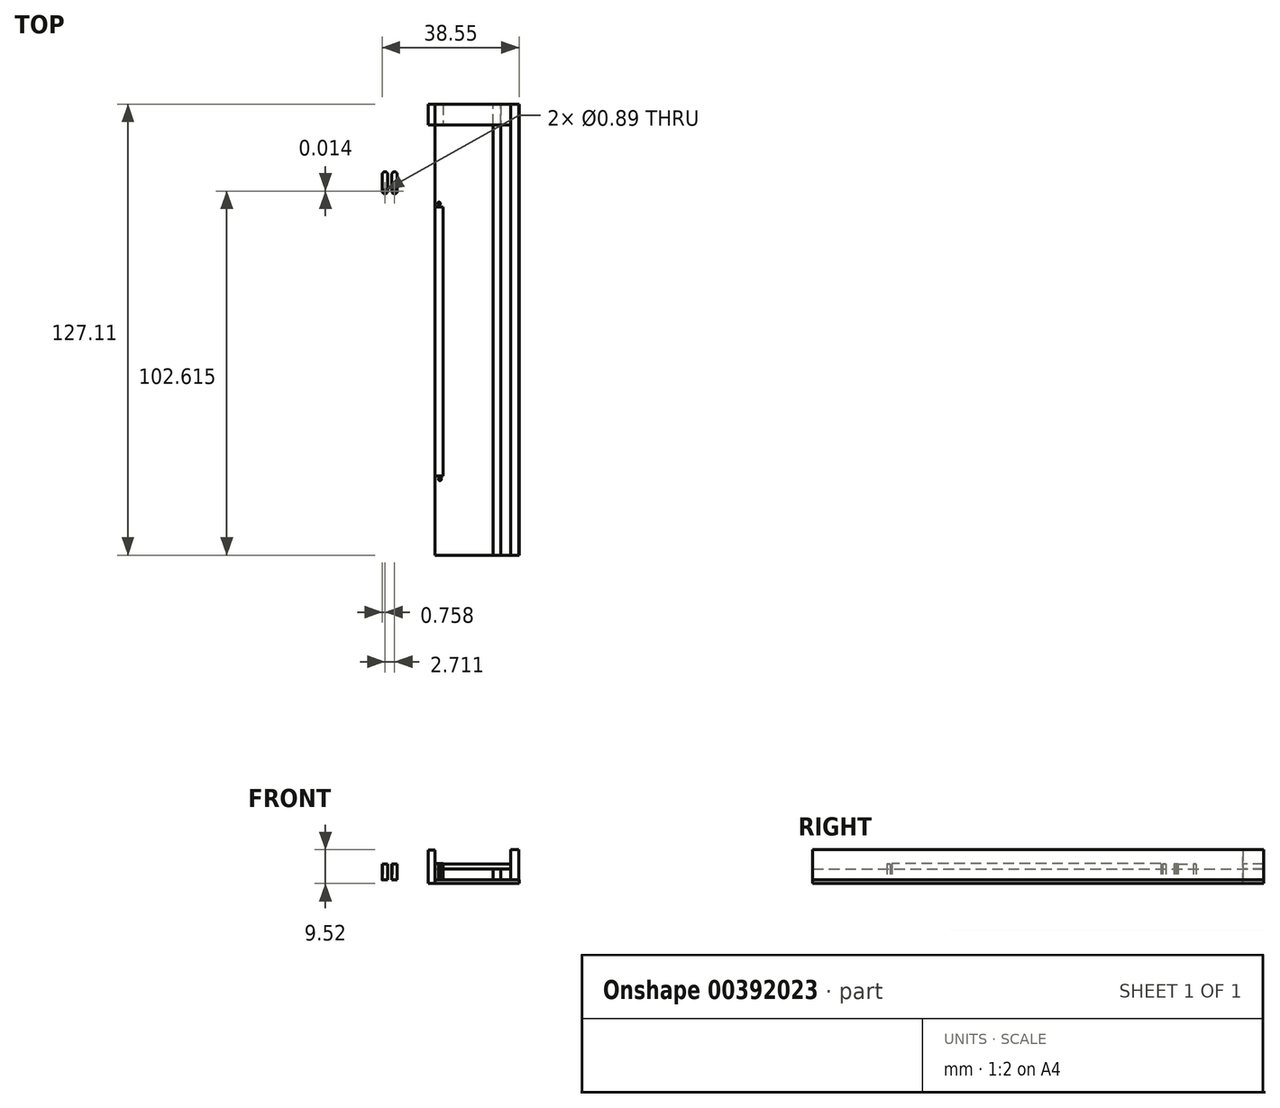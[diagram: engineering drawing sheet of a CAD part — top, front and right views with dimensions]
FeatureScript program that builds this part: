
annotation { "Feature Type Name" : "Feature", "Feature Type Description" : "" }
export const myFeature = defineFeature(function(context is Context, id is Id, definition is map)
    precondition{}
    {
        {
            var Q0;
            Q0=qCreatedBy(makeId("Top.planeOp"),FACE);
            var sketch = newSketch(context, id + "F0", { "sketchPlane" : qUnion([Q0])});
            skLineSegment(sketch, "E0.bottom", {"start": v(-12.76, 61.7) * mm, "end": v(12.87, 61.7) * mm});
            skLineSegment(sketch, "E0.top", {"start": v(-12.76, -65.4) * mm, "end": v(12.87, -65.4) * mm});
            skLineSegment(sketch, "E0.left", {"start": v(-12.76, 61.7) * mm, "end": v(-12.76, -65.4) * mm});
            skLineSegment(sketch, "E0.right", {"start": v(12.87, 61.7) * mm, "end": v(12.87, -65.4) * mm});
            skLineSegment(sketch, "E1", {"start": v(-10.88, 61.7) * mm, "end": v(-10.88, -65.4) * mm});
            skLineSegment(sketch, "E2", {"start": v(10.5, 61.7) * mm, "end": v(10.5, -65.4) * mm});
            skLineSegment(sketch, "E3", {"start": v(7.72, 61.7) * mm, "end": v(7.72, -65.4) * mm});
            skLineSegment(sketch, "E4", {"start": v(5.47, 61.7) * mm, "end": v(5.47, -65.4) * mm});
            skLineSegment(sketch, "E5", {"start": v(-8.47, 61.7) * mm, "end": v(-8.47, 39.44) * mm});
            skLineSegment(sketch, "E6.top", {"start": v(-12.76, 55.9) * mm, "end": v(12.87, 55.9) * mm});
            skLineSegment(sketch, "E6.left", {"start": v(-12.76, 61.7) * mm, "end": v(-12.76, 55.9) * mm});
            skLineSegment(sketch, "E6.right", {"start": v(12.87, 61.7) * mm, "end": v(12.87, 55.9) * mm});
            skLineSegment(sketch, "E7", {"start": v(-8.47, 39.44) * mm, "end": v(-10.88, 39.44) * mm});
            skLineSegment(sketch, "E8", {"start": v(-8.47, 32.73) * mm, "end": v(-10.88, 32.73) * mm});
            skLineSegment(sketch, "E9", {"start": v(-8.47, -43.05) * mm, "end": v(-10.88, -43.05) * mm});
            skLineSegment(sketch, "E10", {"start": v(-8.47, -49.75) * mm, "end": v(-10.88, -49.75) * mm});
            skLineSegment(sketch, "E11.trimOffspring", {"start": v(-8.47, 32.73) * mm, "end": v(-8.47, -43.05) * mm});
            skLineSegment(sketch, "E12.trimOffspring", {"start": v(-8.47, -49.75) * mm, "end": v(-8.47, -65.4) * mm});
            skCircle(sketch, "E13", {"center": v(-9.7, 33.72) * mm, "radius": 0.44 * mm});
            skArc(sketch, "E14", {"start": v(-10.46, 33.78) * mm, "mid": v(-9.7, 32.96) * mm, "end": v(-8.95, 33.78) * mm});
            skLineSegment(sketch, "E15", {"start": v(-8.95, 33.78) * mm, "end": v(-8.95, 38.42) * mm});
            skLineSegment(sketch, "E16", {"start": v(-10.46, 33.78) * mm, "end": v(-10.46, 38.4) * mm});
            skArc(sketch, "E17", {"start": v(-8.95, 38.42) * mm, "mid": v(-9.71, 39.18) * mm, "end": v(-10.46, 38.4) * mm});
            skCircle(sketch, "E18", {"center": v(-9.7, 33.72) * mm, "radius": 0.41 * mm});
            skCircle(sketch, "E19", {"center": v(-9.45, -43.97) * mm, "radius": 0.44 * mm});
            skArc(sketch, "E20", {"start": v(-8.7, -44.03) * mm, "mid": v(-9.44, -43.21) * mm, "end": v(-10.2, -44.02) * mm});
            skLineSegment(sketch, "E21", {"start": v(-10.2, -44.02) * mm, "end": v(-10.2, -48.67) * mm});
            skLineSegment(sketch, "E22", {"start": v(-8.7, -44.03) * mm, "end": v(-8.7, -48.65) * mm});
            skArc(sketch, "E23", {"start": v(-10.2, -48.67) * mm, "mid": v(-9.44, -49.43) * mm, "end": v(-8.7, -48.65) * mm});
            skCircle(sketch, "E24", {"center": v(-9.45, -43.97) * mm, "radius": 0.41 * mm});
            skSolve(sketch);
        }
        {
            var Q0;
            Q0=qCreatedBy(makeId("Top.planeOp"),FACE);
            var sketch = newSketch(context, id + "F1", { "sketchPlane" : qUnion([Q0])});
            skCircle(sketch, "E25", {"center": v(-24.92, 37.23) * mm, "radius": 0.44 * mm});
            skArc(sketch, "E26", {"start": v(-25.68, 37.3) * mm, "mid": v(-24.93, 36.47) * mm, "end": v(-24.17, 37.28) * mm});
            skLineSegment(sketch, "E27", {"start": v(-24.17, 37.28) * mm, "end": v(-24.17, 41.93) * mm});
            skLineSegment(sketch, "E28", {"start": v(-25.68, 37.3) * mm, "end": v(-25.68, 41.9) * mm});
            skArc(sketch, "E29", {"start": v(-24.17, 41.93) * mm, "mid": v(-24.93, 42.69) * mm, "end": v(-25.68, 41.9) * mm});
            skCircle(sketch, "E30", {"center": v(-22.21, 37.22) * mm, "radius": 0.44 * mm});
            skArc(sketch, "E31", {"start": v(-22.97, 37.28) * mm, "mid": v(-22.22, 36.46) * mm, "end": v(-21.46, 37.27) * mm});
            skLineSegment(sketch, "E32", {"start": v(-21.46, 37.27) * mm, "end": v(-21.46, 41.92) * mm});
            skLineSegment(sketch, "E33", {"start": v(-22.97, 37.28) * mm, "end": v(-22.97, 41.9) * mm});
            skArc(sketch, "E34", {"start": v(-21.46, 41.92) * mm, "mid": v(-22.22, 42.67) * mm, "end": v(-22.97, 41.9) * mm});
            skSolve(sketch);
        }
        {
            var Q0;
            Q0=qCreatedBy(makeId("Right.planeOp"),FACE);
            var sketch = newSketch(context, id + "F2", { "sketchPlane" : qUnion([Q0])});
            skLineSegment(sketch, "E35.bottom", {"start": v(61.7, 8.5) * mm, "end": v(-65.36, 8.5) * mm});
            skLineSegment(sketch, "E35.top", {"start": v(61.7, 0) * mm, "end": v(-65.36, 0) * mm});
            skLineSegment(sketch, "E35.left", {"start": v(61.7, 8.5) * mm, "end": v(61.7, 0) * mm});
            skLineSegment(sketch, "E35.right", {"start": v(-65.36, 8.5) * mm, "end": v(-65.36, 0) * mm});
            skSolve(sketch);
        }
        {
            var Q0;
            Q0=qCreatedBy(makeId("Front.planeOp"),FACE);
            var sketch = newSketch(context, id + "F3", { "sketchPlane" : qUnion([Q0])});
            skLineSegment(sketch, "E36.bottom", {"start": v(7.75, 0) * mm, "end": v(5.5, 0) * mm});
            skLineSegment(sketch, "E36.right", {"start": v(5.5, 0) * mm, "end": v(5.5, 3.08) * mm});
            skLineSegment(sketch, "E37", {"start": v(7.75, 0) * mm, "end": v(7.75, 3.08) * mm});
            skLineSegment(sketch, "E38.trimOffspring", {"start": v(7.75, 3.08) * mm, "end": v(5.5, 3.08) * mm});
            skLineSegment(sketch, "E39.bottom", {"start": v(-8.47, 0) * mm, "end": v(-10.87, 0) * mm});
            skLineSegment(sketch, "E39.top", {"start": v(-8.47, 3.08) * mm, "end": v(-10.87, 3.08) * mm});
            skLineSegment(sketch, "E39.left", {"start": v(-8.47, 0) * mm, "end": v(-8.47, 3.08) * mm});
            skLineSegment(sketch, "E39.right", {"start": v(-10.87, 0) * mm, "end": v(-10.87, 3.08) * mm});
            skPoint(sketch, "E40.orphan", {"position": v(12.85, 0) * mm});
            skLineSegment(sketch, "E41.bottom", {"start": v(7.75, 3.08) * mm, "end": v(-10.87, 3.08) * mm});
            skLineSegment(sketch, "E41.top", {"start": v(7.75, 4.56) * mm, "end": v(-10.87, 4.56) * mm});
            skLineSegment(sketch, "E41.left", {"start": v(7.75, 3.08) * mm, "end": v(7.75, 4.56) * mm});
            skLineSegment(sketch, "E41.right", {"start": v(-10.87, 3.08) * mm, "end": v(-10.87, 4.56) * mm});
            skSolve(sketch);
        }
        {
            var Q0;
            Q0 = qSketchRegion(id + "F2", true);
            extrude(context, id + "F4", {"entities" : qUnion([Q0]), "depth" : 12.83 * mm, "hasSecondDirection" : true, "secondDirectionOppositeDirection" : false, "secondDirectionDepth" : 10.5 * mm});
        }
        {
            var Q0;
            Q0=makeQuery(id+"F3.imprint","IMPRINT",FACE,{"disambiguationData":[TD([[makeQuery(id+"F3.imprint","IMPRINT",EDGE,{"derivedFrom":sQuery(id+"F3.wireOp",EDGE,"E36.bottom")}),-1.0]])]});
            extrude(context, id + "F5", {"entities" : qUnion([Q0]), "depth" : 65.38 * mm, "hasSecondDirection" : true, "secondDirectionOppositeDirection" : true, "secondDirectionDepth" : 61.7 * mm});
        }
        {
            var Q0;
            Q0=makeQuery(id+"F0.imprint","IMPRINT",FACE,{"disambiguationData":[TD([[makeQuery(id+"F0.imprint","IMPRINT",EDGE,{"derivedFrom":sQuery(id+"F0.wireOp",EDGE,"E18")}),1.0]])]});
            var Q1;
            Q1=makeQuery(id+"F0.imprint","IMPRINT",FACE,{"disambiguationData":[TD([[makeQuery(id+"F0.imprint","IMPRINT",EDGE,{"derivedFrom":sQuery(id+"F0.wireOp",EDGE,"E13")}),-1.0]])]});
            var Q2;
            Q2=makeQuery(id+"F0.imprint","IMPRINT",FACE,{"disambiguationData":[TD([[makeQuery(id+"F0.imprint","IMPRINT",EDGE,{"derivedFrom":sQuery(id+"F0.wireOp",EDGE,"E13")}),1.0]])]});
            var Q3;
            {var subQ4=sQuery(id+"F0.wireOp",EDGE,"E0.left");Q3=makeQuery(id+"F0.imprint","IMPRINT",FACE,{"disambiguationData":[TD([[makeQuery(id+"F0.imprint","IMPRINT",EDGE,{"derivedFrom":subQ4}),1.0]])]});}
            var Q4;
            {var subQ0=sQuery(id+"F0.wireOp",EDGE,"E7");Q4=makeQuery(id+"F0.imprint","IMPRINT",FACE,{"disambiguationData":[TD([[makeQuery(id+"F0.imprint","IMPRINT",EDGE,{"derivedFrom":subQ0}),-1.0]])]});}
            var Q5;
            {var subQ0=sQuery(id+"F0.wireOp",EDGE,"E8");Q5=makeQuery(id+"F0.imprint","IMPRINT",FACE,{"disambiguationData":[TD([[makeQuery(id+"F0.imprint","IMPRINT",EDGE,{"derivedFrom":subQ0}),1.0]])]});}
            var Q6;
            {var subQ3=sQuery(id+"F0.wireOp",EDGE,"E7");Q6=makeQuery(id+"F0.imprint","IMPRINT",FACE,{"disambiguationData":[TD([[makeQuery(id+"F0.imprint","IMPRINT",EDGE,{"derivedFrom":subQ3}),1.0]])]});}
            var Q7;
            {var subQ0=sQuery(id+"F0.wireOp",EDGE,"E0.bottom");var subQ1=sQuery(id+"F0.wireOp",EDGE,"E4");var subQ2=makeQuery(id+"F0.imprint","INTERSECT",VERTEX,{"derivedFrom":[subQ1,subQ0]});Q7=makeQuery(id+"F0.imprint","IMPRINT",FACE,{"disambiguationData":[TD([[makeQuery(id+"F0.imprint","IMPRINT",EDGE,{"disambiguationData":[TD([[subQ2,-1.0]])],"derivedFrom":subQ1}),-1.0]])]});}
            var Q8;
            {var subQ0=sQuery(id+"F0.wireOp",EDGE,"E0.bottom");var subQ1=sQuery(id+"F0.wireOp",EDGE,"E1");var subQ2=makeQuery(id+"F0.imprint","INTERSECT",VERTEX,{"derivedFrom":[subQ1,subQ0]});Q8=makeQuery(id+"F0.imprint","IMPRINT",FACE,{"disambiguationData":[TD([[makeQuery(id+"F0.imprint","IMPRINT",EDGE,{"disambiguationData":[TD([[subQ2,-1.0]])],"derivedFrom":subQ1}),1.0]])]});}
            var Q9;
            {var subQ5=sQuery(id+"F0.wireOp",EDGE,"E6.left");Q9=makeQuery(id+"F0.imprint","IMPRINT",FACE,{"disambiguationData":[TD([[makeQuery(id+"F0.imprint","IMPRINT",EDGE,{"derivedFrom":subQ5}),1.0]])]});}
            var Q10;
            {var subQ0=sQuery(id+"F0.wireOp",EDGE,"E0.bottom");var subQ1=sQuery(id+"F0.wireOp",EDGE,"E3");var subQ2=makeQuery(id+"F0.imprint","INTERSECT",VERTEX,{"derivedFrom":[subQ1,subQ0]});Q10=makeQuery(id+"F0.imprint","IMPRINT",FACE,{"disambiguationData":[TD([[makeQuery(id+"F0.imprint","IMPRINT",EDGE,{"disambiguationData":[TD([[subQ2,-1.0]])],"derivedFrom":subQ1}),-1.0]])]});}
            var Q11;
            {var subQ0=sQuery(id+"F0.wireOp",EDGE,"E0.bottom");var subQ1=sQuery(id+"F0.wireOp",EDGE,"E2");var subQ2=makeQuery(id+"F0.imprint","INTERSECT",VERTEX,{"derivedFrom":[subQ1,subQ0]});Q11=makeQuery(id+"F0.imprint","IMPRINT",FACE,{"disambiguationData":[TD([[makeQuery(id+"F0.imprint","IMPRINT",EDGE,{"disambiguationData":[TD([[subQ2,-1.0]])],"derivedFrom":subQ1}),-1.0]])]});}
            var Q12;
            {var subQ0=sQuery(id+"F0.wireOp",EDGE,"E2");var subQ1=sQuery(id+"F0.wireOp",EDGE,"E0.top");var subQ2=makeQuery(id+"F0.imprint","INTERSECT",VERTEX,{"derivedFrom":[subQ1,subQ0]});Q12=makeQuery(id+"F0.imprint","IMPRINT",FACE,{"disambiguationData":[TD([[makeQuery(id+"F0.imprint","IMPRINT",EDGE,{"disambiguationData":[TD([[subQ2,1.0]])],"derivedFrom":subQ1}),1.0]])]});}
            var Q13;
            {var subQ0=sQuery(id+"F0.wireOp",EDGE,"E0.right");Q13=makeQuery(id+"F0.imprint","IMPRINT",FACE,{"disambiguationData":[TD([[makeQuery(id+"F0.imprint","IMPRINT",EDGE,{"derivedFrom":subQ0}),-1.0]])]});}
            var Q14;
            {var subQ5=sQuery(id+"F0.wireOp",EDGE,"E6.right");Q14=makeQuery(id+"F0.imprint","IMPRINT",FACE,{"disambiguationData":[TD([[makeQuery(id+"F0.imprint","IMPRINT",EDGE,{"derivedFrom":subQ5}),-1.0]])]});}
            var Q15;
            Q15=makeQuery(id+"F0.imprint","IMPRINT",FACE,{"disambiguationData":[TD([[makeQuery(id+"F0.imprint","IMPRINT",EDGE,{"derivedFrom":sQuery(id+"F0.wireOp",EDGE,"E19")}),-1.0]])]});
            var Q16;
            {var subQ4=sQuery(id+"F0.wireOp",EDGE,"E10");Q16=makeQuery(id+"F0.imprint","IMPRINT",FACE,{"disambiguationData":[TD([[makeQuery(id+"F0.imprint","IMPRINT",EDGE,{"derivedFrom":subQ4}),1.0]])]});}
            var Q17;
            Q17=makeQuery(id+"F0.imprint","IMPRINT",FACE,{"disambiguationData":[TD([[makeQuery(id+"F0.imprint","IMPRINT",EDGE,{"derivedFrom":sQuery(id+"F0.wireOp",EDGE,"E24")}),1.0]])]});
            var Q18;
            Q18=makeQuery(id+"F0.imprint","IMPRINT",FACE,{"disambiguationData":[TD([[makeQuery(id+"F0.imprint","IMPRINT",EDGE,{"derivedFrom":sQuery(id+"F0.wireOp",EDGE,"E19")}),1.0]])]});
            var Q19;
            {var subQ0=sQuery(id+"F0.wireOp",EDGE,"E3");var subQ1=sQuery(id+"F0.wireOp",EDGE,"E0.top");var subQ2=makeQuery(id+"F0.imprint","INTERSECT",VERTEX,{"derivedFrom":[subQ1,subQ0]});Q19=makeQuery(id+"F0.imprint","IMPRINT",FACE,{"disambiguationData":[TD([[makeQuery(id+"F0.imprint","IMPRINT",EDGE,{"disambiguationData":[TD([[subQ2,1.0]])],"derivedFrom":subQ1}),1.0]])]});}
            extrude(context, id + "F6", {"entities" : qUnion([Q0, Q1, Q2, Q3, Q4, Q5, Q6, Q7, Q8, Q9, Q10, Q11, Q12, Q13, Q14, Q15, Q16, Q17, Q18, Q19]), "oppositeDirection" : true, "depth" : 1.02 * mm});
        }
        {
            var Q0;
            {var subQ4=sQuery(id+"F0.wireOp",EDGE,"E0.left");Q0=makeQuery(id+"F0.imprint","IMPRINT",FACE,{"disambiguationData":[TD([[makeQuery(id+"F0.imprint","IMPRINT",EDGE,{"derivedFrom":subQ4}),1.0]])]});}
            var Q1;
            {var subQ5=sQuery(id+"F0.wireOp",EDGE,"E6.left");Q1=makeQuery(id+"F0.imprint","IMPRINT",FACE,{"disambiguationData":[TD([[makeQuery(id+"F0.imprint","IMPRINT",EDGE,{"derivedFrom":subQ5}),1.0]])]});}
            extrude(context, id + "F7", {"entities" : qUnion([Q0, Q1]), "operationType" : NewBodyOperationType.ADD, "depth" : 8.38 * mm});
        }
        {
            var Q0;
            Q0=makeQuery(id+"F0.imprint","IMPRINT",FACE,{"disambiguationData":[TD([[makeQuery(id+"F0.imprint","IMPRINT",EDGE,{"derivedFrom":sQuery(id+"F0.wireOp",EDGE,"E24")}),1.0]])]});
            var Q1;
            Q1=makeQuery(id+"F0.imprint","IMPRINT",FACE,{"disambiguationData":[TD([[makeQuery(id+"F0.imprint","IMPRINT",EDGE,{"derivedFrom":sQuery(id+"F0.wireOp",EDGE,"E18")}),1.0]])]});
            extrude(context, id + "F8", {"entities" : qUnion([Q0, Q1]), "operationType" : NewBodyOperationType.ADD, "depth" : 4.55 * mm});
        }
        {
            var Q0;
            {var subQ0=sQuery(id+"F0.wireOp",EDGE,"E8");Q0=makeQuery(id+"F0.imprint","IMPRINT",FACE,{"disambiguationData":[TD([[makeQuery(id+"F0.imprint","IMPRINT",EDGE,{"derivedFrom":subQ0}),1.0]])]});}
            extrude(context, id + "F9", {"entities" : qUnion([Q0]), "operationType" : NewBodyOperationType.ADD, "depth" : 4.56 * mm});
        }
        {
            var Q0;
            Q0=makeQuery(id+"F1.imprint","IMPRINT",FACE,{"disambiguationData":[TD([[makeQuery(id+"F1.imprint","IMPRINT",EDGE,{"derivedFrom":sQuery(id+"F1.wireOp",EDGE,"E30")}),-1.0]])]});
            var Q1;
            Q1=makeQuery(id+"F1.imprint","IMPRINT",FACE,{"disambiguationData":[TD([[makeQuery(id+"F1.imprint","IMPRINT",EDGE,{"derivedFrom":sQuery(id+"F1.wireOp",EDGE,"E25")}),-1.0]])]});
            extrude(context, id + "F10", {"entities" : qUnion([Q0, Q1]), "depth" : 4.52 * mm});
        }
        {
            var Q0;
            {var subQ0=sQuery(id+"F0.wireOp",EDGE,"E0.bottom");var subQ1=sQuery(id+"F0.wireOp",EDGE,"E2");var subQ2=makeQuery(id+"F0.imprint","INTERSECT",VERTEX,{"derivedFrom":[subQ1,subQ0]});Q0=makeQuery(id+"F0.imprint","IMPRINT",FACE,{"disambiguationData":[TD([[makeQuery(id+"F0.imprint","IMPRINT",EDGE,{"disambiguationData":[TD([[subQ2,-1.0]])],"derivedFrom":subQ1}),-1.0]])]});}
            var Q1;
            {var subQ0=sQuery(id+"F0.wireOp",EDGE,"E0.bottom");var subQ1=sQuery(id+"F0.wireOp",EDGE,"E3");var subQ2=makeQuery(id+"F0.imprint","INTERSECT",VERTEX,{"derivedFrom":[subQ1,subQ0]});Q1=makeQuery(id+"F0.imprint","IMPRINT",FACE,{"disambiguationData":[TD([[makeQuery(id+"F0.imprint","IMPRINT",EDGE,{"disambiguationData":[TD([[subQ2,-1.0]])],"derivedFrom":subQ1}),-1.0]])]});}
            var Q2;
            {var subQ0=sQuery(id+"F0.wireOp",EDGE,"E0.bottom");var subQ1=sQuery(id+"F0.wireOp",EDGE,"E4");var subQ2=makeQuery(id+"F0.imprint","INTERSECT",VERTEX,{"derivedFrom":[subQ1,subQ0]});Q2=makeQuery(id+"F0.imprint","IMPRINT",FACE,{"disambiguationData":[TD([[makeQuery(id+"F0.imprint","IMPRINT",EDGE,{"disambiguationData":[TD([[subQ2,-1.0]])],"derivedFrom":subQ1}),-1.0]])]});}
            var Q3;
            {var subQ0=sQuery(id+"F0.wireOp",EDGE,"E0.bottom");var subQ1=sQuery(id+"F0.wireOp",EDGE,"E1");var subQ2=makeQuery(id+"F0.imprint","INTERSECT",VERTEX,{"derivedFrom":[subQ1,subQ0]});Q3=makeQuery(id+"F0.imprint","IMPRINT",FACE,{"disambiguationData":[TD([[makeQuery(id+"F0.imprint","IMPRINT",EDGE,{"disambiguationData":[TD([[subQ2,-1.0]])],"derivedFrom":subQ1}),1.0]])]});}
            extrude(context, id + "F11", {"entities" : qUnion([Q0, Q1, Q2, Q3]), "depth" : 4.55 * mm, "hasSecondDirection" : true, "secondDirectionOppositeDirection" : false, "secondDirectionDepth" : 3.1 * mm});
        }
        {
            var Q0;
            {var subQ0=sQuery(id+"F0.wireOp",EDGE,"E0.bottom");var subQ1=sQuery(id+"F0.wireOp",EDGE,"E1");var subQ2=makeQuery(id+"F0.imprint","INTERSECT",VERTEX,{"derivedFrom":[subQ1,subQ0]});Q0=makeQuery(id+"F0.imprint","IMPRINT",FACE,{"disambiguationData":[TD([[makeQuery(id+"F0.imprint","IMPRINT",EDGE,{"disambiguationData":[TD([[subQ2,-1.0]])],"derivedFrom":subQ1}),1.0]])]});}
            extrude(context, id + "F12", {"entities" : qUnion([Q0]), "operationType" : NewBodyOperationType.ADD, "depth" : 3.07 * mm});
        }
        {
            var Q0;
            {var subQ0=sQuery(id+"F0.wireOp",EDGE,"E0.bottom");var subQ1=sQuery(id+"F0.wireOp",EDGE,"E2");var subQ2=makeQuery(id+"F0.imprint","INTERSECT",VERTEX,{"derivedFrom":[subQ1,subQ0]});Q0=makeQuery(id+"F0.imprint","IMPRINT",FACE,{"disambiguationData":[TD([[makeQuery(id+"F0.imprint","IMPRINT",EDGE,{"disambiguationData":[TD([[subQ2,-1.0]])],"derivedFrom":subQ1}),-1.0]])]});}
            extrude(context, id + "F13", {"entities" : qUnion([Q0]), "depth" : 3.1 * mm});
        }
    });
